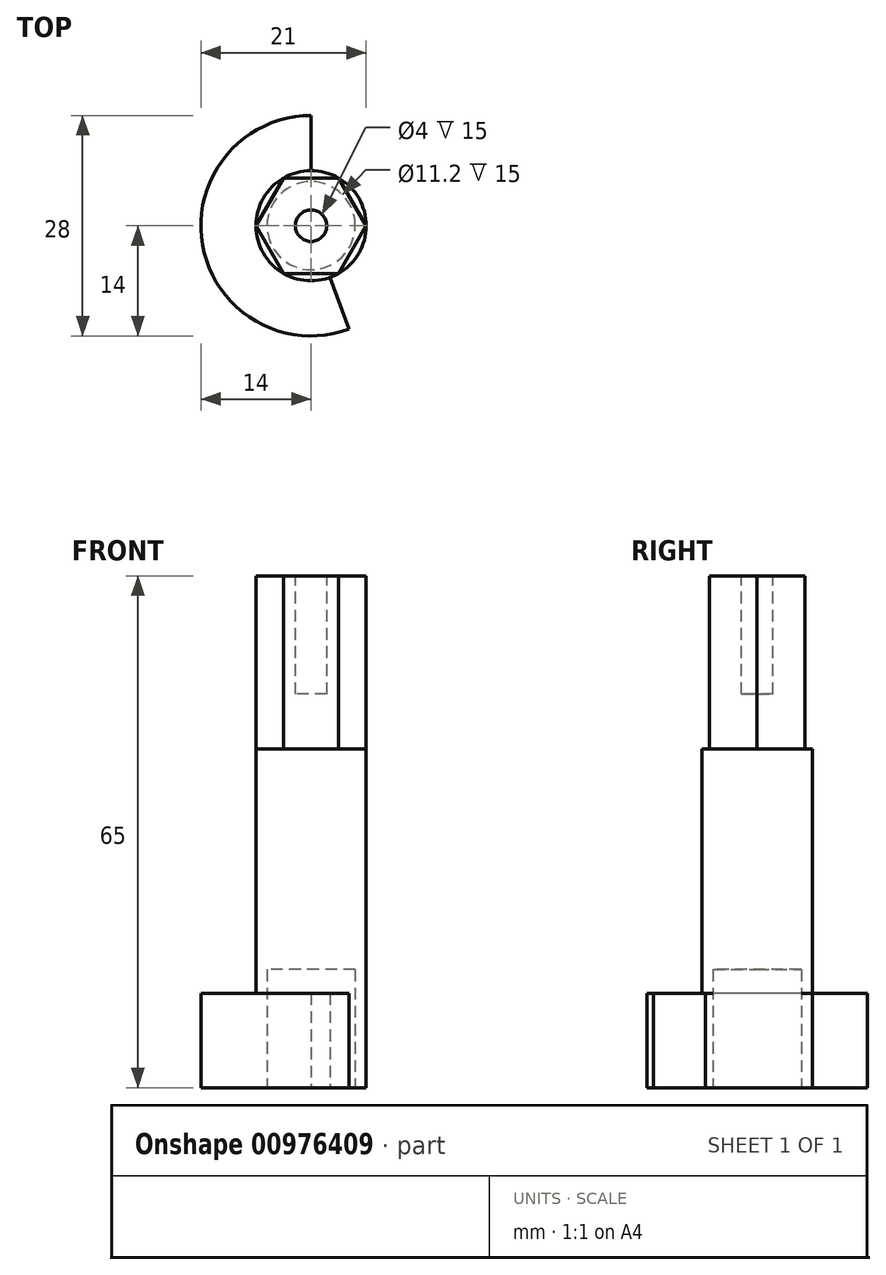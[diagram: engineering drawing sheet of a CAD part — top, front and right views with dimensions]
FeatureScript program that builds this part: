
annotation { "Feature Type Name" : "Feature", "Feature Type Description" : "" }
export const myFeature = defineFeature(function(context is Context, id is Id, definition is map)
    precondition{}
    {
        {
            var Q0;
            Q0=qCreatedBy(makeId("Top.planeOp"),FACE);
            var sketch = newSketch(context, id + "F0", { "sketchPlane" : qUnion([Q0])});
            skCircle(sketch, "E0", {"center": v(0, 0) * mm, "radius": 7 * mm});
            skCircle(sketch, "E1.0", {"center": v(0, 0) * mm, "radius": 5.6 * mm});
            skArc(sketch, "E2", {"start": v(0, 14) * mm, "mid": v(-13.79, -2.43) * mm, "end": v(4.79, -13.16) * mm});
            skLineSegment(sketch, "E3", {"start": v(0, 0) * mm, "end": v(0, 14) * mm});
            skLineSegment(sketch, "E4", {"start": v(0, 0) * mm, "end": v(4.79, -13.16) * mm});
            skSolve(sketch);
        }
        {
            var Q0;
            Q0 = qSketchRegion(id + "F0", true);
            extrude(context, id + "F1", {"entities" : qUnion([Q0]), "depth" : 12 * mm, "offsetDistance" : 25 * mm});
        }
        {
            var Q0;
            {var subQ0=sQuery(id+"F0.wireOp",EDGE,"E3");var subQ1=sQuery(id+"F0.wireOp",EDGE,"E1.0");var subQ2=makeQuery(id+"F0.imprint","INTERSECT",VERTEX,{"derivedFrom":[subQ1,subQ0]});Q0=makeQuery(id+"F0.imprint","IMPRINT",FACE,{"disambiguationData":[TD([[makeQuery(id+"F0.imprint","IMPRINT",EDGE,{"disambiguationData":[TD([[subQ2,1.0]])],"derivedFrom":subQ1}),1.0]])]});}
            var Q1;
            {var subQ0=sQuery(id+"F0.wireOp",EDGE,"E3");var subQ1=sQuery(id+"F0.wireOp",EDGE,"E1.0");var subQ2=makeQuery(id+"F0.imprint","INTERSECT",VERTEX,{"derivedFrom":[subQ1,subQ0]});Q1=makeQuery(id+"F0.imprint","IMPRINT",FACE,{"disambiguationData":[TD([[makeQuery(id+"F0.imprint","IMPRINT",EDGE,{"disambiguationData":[TD([[subQ2,-1.0]])],"derivedFrom":subQ1}),1.0]])]});}
            var Q2;
            {var subQ0=sQuery(id+"F0.wireOp",EDGE,"E3");var subQ1=sQuery(id+"F0.wireOp",EDGE,"E0");var subQ2=makeQuery(id+"F0.imprint","INTERSECT",VERTEX,{"derivedFrom":[subQ1,subQ0]});Q2=makeQuery(id+"F0.imprint","IMPRINT",FACE,{"disambiguationData":[TD([[makeQuery(id+"F0.imprint","IMPRINT",EDGE,{"disambiguationData":[TD([[subQ2,1.0]])],"derivedFrom":subQ1}),1.0]])]});}
            var Q3;
            {var subQ0=sQuery(id+"F0.wireOp",EDGE,"E3");var subQ1=sQuery(id+"F0.wireOp",EDGE,"E0");var subQ2=makeQuery(id+"F0.imprint","INTERSECT",VERTEX,{"derivedFrom":[subQ1,subQ0]});Q3=makeQuery(id+"F0.imprint","IMPRINT",FACE,{"disambiguationData":[TD([[makeQuery(id+"F0.imprint","IMPRINT",EDGE,{"disambiguationData":[TD([[subQ2,-1.0]])],"derivedFrom":subQ1}),1.0]])]});}
            extrude(context, id + "F2", {"entities" : qUnion([Q0, Q1, Q2, Q3]), "operationType" : NewBodyOperationType.ADD, "depth" : 43 * mm, "offsetDistance" : 25 * mm});
        }
        {
            var Q0;
            Q0=makeQuery(id+"F2.opExtrude","CAP_FACE",FACE,{"disambiguationData":[OSD([sQuery(id+"F0.wireOp",EDGE,"E0")])],"isStart":false});
            var sketch = newSketch(context, id + "F3", { "sketchPlane" : qUnion([Q0])});
            skCircle(sketch, "E5.cCircle", {"center": v(0, 0) * mm, "radius": 7 * mm, "construction": true});
            skLineSegment(sketch, "E5.0", {"start": v(3.5, 6.06) * mm, "end": v(7, 0) * mm});
            skLineSegment(sketch, "E5.1", {"start": v(7, 0) * mm, "end": v(3.5, -6.06) * mm});
            skLineSegment(sketch, "E5.2", {"start": v(3.5, -6.06) * mm, "end": v(-3.5, -6.06) * mm});
            skLineSegment(sketch, "E5.3", {"start": v(-3.5, -6.06) * mm, "end": v(-7, 0) * mm});
            skLineSegment(sketch, "E5.4", {"start": v(-7, 0) * mm, "end": v(-3.5, 6.06) * mm});
            skLineSegment(sketch, "E5.5", {"start": v(-3.5, 6.06) * mm, "end": v(3.5, 6.06) * mm});
            skSolve(sketch);
        }
        {
            var Q0;
            Q0 = qSketchRegion(id + "F3", true);
            extrude(context, id + "F4", {"entities" : qUnion([Q0]), "operationType" : NewBodyOperationType.ADD, "depth" : 22 * mm, "offsetDistance" : 25 * mm});
        }
        {
            var Q0;
            Q0=makeQuery(id+"F4.opExtrude","CAP_FACE",FACE,{"disambiguationData":[OSD([sQuery(id+"F3.wireOp",EDGE,"E5.0"),sQuery(id+"F3.wireOp",EDGE,"E5.1"),sQuery(id+"F3.wireOp",EDGE,"E5.2"),sQuery(id+"F3.wireOp",EDGE,"E5.3"),sQuery(id+"F3.wireOp",EDGE,"E5.4"),sQuery(id+"F3.wireOp",EDGE,"E5.5")])],"isStart":false});
            var sketch = newSketch(context, id + "F5", { "sketchPlane" : qUnion([Q0])});
            skCircle(sketch, "E6", {"center": v(0, 0) * mm, "radius": 2 * mm});
            skSolve(sketch);
        }
        {
            var Q0;
            Q0 = qSketchRegion(id + "F5", true);
            extrude(context, id + "F6", {"entities" : qUnion([Q0]), "operationType" : NewBodyOperationType.REMOVE, "oppositeDirection" : true, "depth" : 15 * mm, "offsetDistance" : 25 * mm});
        }
        {
            var Q0;
            {var subQ0=sQuery(id+"F0.wireOp",EDGE,"E3");var subQ1=sQuery(id+"F0.wireOp",EDGE,"E1.0");var subQ2=makeQuery(id+"F0.imprint","INTERSECT",VERTEX,{"derivedFrom":[subQ1,subQ0]});Q0=makeQuery(id+"F0.imprint","IMPRINT",FACE,{"disambiguationData":[TD([[makeQuery(id+"F0.imprint","IMPRINT",EDGE,{"disambiguationData":[TD([[subQ2,1.0]])],"derivedFrom":subQ1}),1.0]])]});}
            var Q1;
            {var subQ0=sQuery(id+"F0.wireOp",EDGE,"E3");var subQ1=sQuery(id+"F0.wireOp",EDGE,"E1.0");var subQ2=makeQuery(id+"F0.imprint","INTERSECT",VERTEX,{"derivedFrom":[subQ1,subQ0]});Q1=makeQuery(id+"F0.imprint","IMPRINT",FACE,{"disambiguationData":[TD([[makeQuery(id+"F0.imprint","IMPRINT",EDGE,{"disambiguationData":[TD([[subQ2,-1.0]])],"derivedFrom":subQ1}),1.0]])]});}
            extrude(context, id + "F7", {"entities" : qUnion([Q0, Q1]), "operationType" : NewBodyOperationType.REMOVE, "depth" : 15 * mm, "offsetDistance" : 25 * mm});
        }
    });
